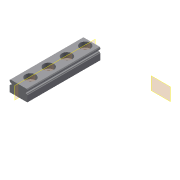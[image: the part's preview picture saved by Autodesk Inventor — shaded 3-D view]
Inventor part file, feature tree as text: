
AUTODESK INVENTOR PART (.ipt)
format: ipt  version: 2019.4 (Build 234330000, 330)  size: 167,424 bytes
history: native  units: mm
features: plane x2, sketch x2, other x2, extrude x1, mirror x1, hole x1, pattern_linear x1, projected_geometry x1
ambient origin geometry x8: Origin, YZ Plane, XZ Plane, XY Plane, X Axis, Y Axis, Z Axis, Center Point
bodies: Solid1 (feature_tree)
feature tree (11):
  plane  "Work Plane1"
  extrude  "Extrusion1"  Depth=0.5mm
  mirror  "Mirror1"
  hole  "Hole1"  [1 undecoded]
  pattern_linear  "Rectangular Pattern1"  Spacing1=6.05mm  [1 undecoded]
  plane  "Work Plane2"
  sketch  "Sketch1"  dims[d0=0.5mm d1=0.5mm]
  sketch  "Sketch2"  dims[d4=50.0mm d5=0.0mm d6=3.5mm d7=6.0mm d8=7.0mm d9=3.5mm d10=90.0deg d11=8.0mm d12=20.594885mm d13=50.0mm d15=12.5mm d17=6.05mm d18=7.8mm d20=2.67563mm d21=0.5mm d22=1.1mm d23=4.7mm d24=0.227539mm d25=0.228mm d26=0.0mm d27=0.248315mm d28=0.218573mm]
  projected_geometry  "Projected Loop1"
  other  "Assembly_Cube_Z_Focus_MGN_NEMA_v3.iam"
  other  "00_MGN12 LINEAR GUIDE RAIL, CONFIGURABLE:1"
note: 2 required parameter values undecoded (feature->parameter linkage not recoverable at this tier; creation-order binding heuristic only, values carry confidence <= 0.55)
